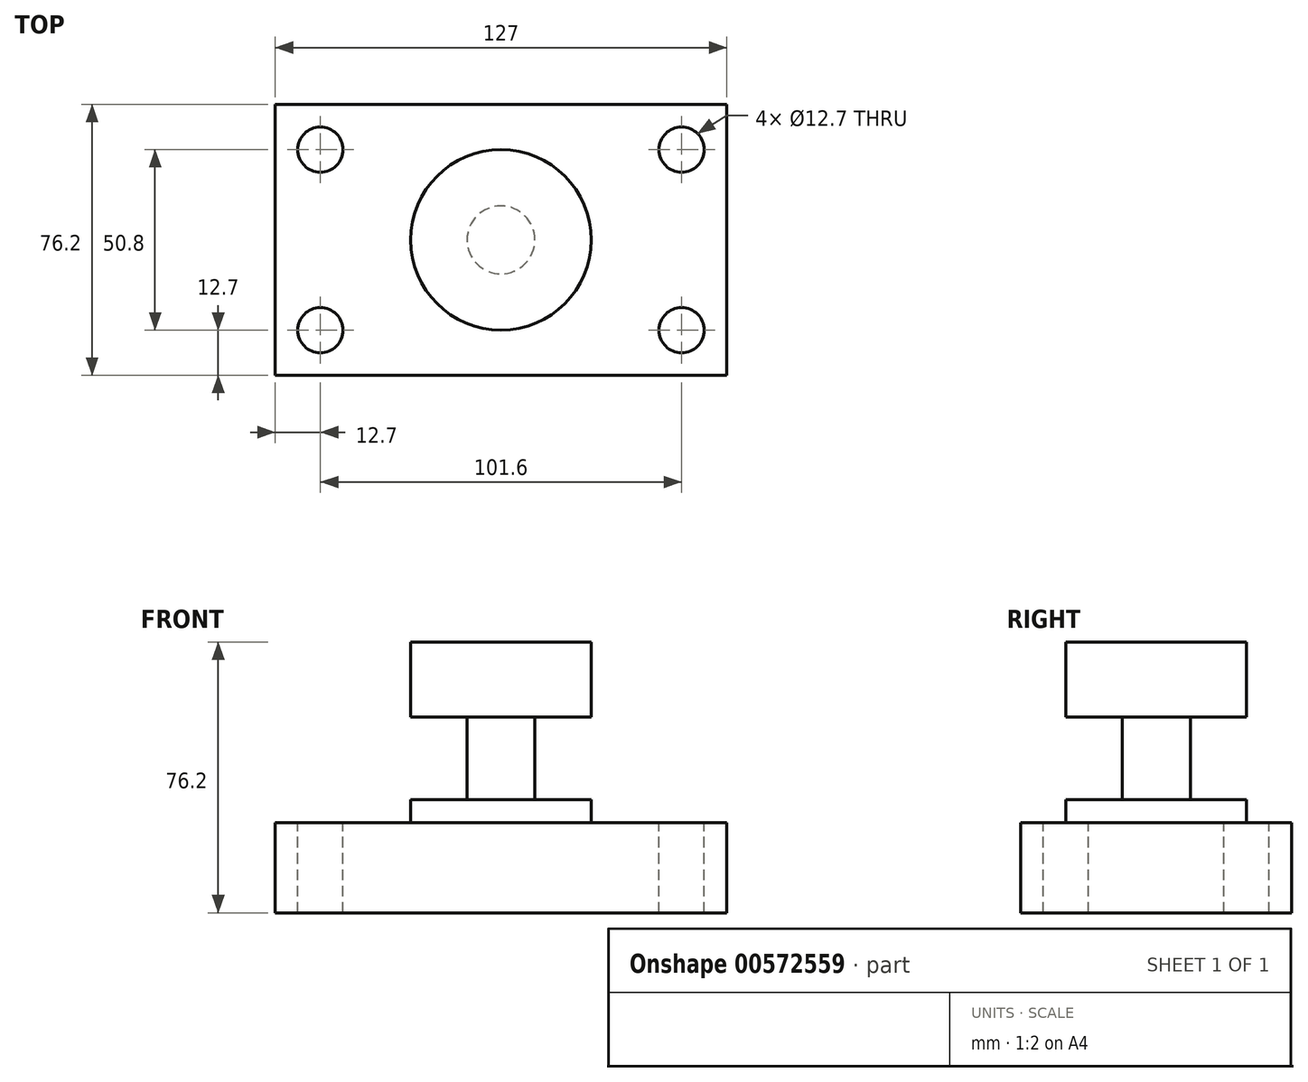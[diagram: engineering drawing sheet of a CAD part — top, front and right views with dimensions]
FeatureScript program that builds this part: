
annotation { "Feature Type Name" : "Feature", "Feature Type Description" : "" }
export const myFeature = defineFeature(function(context is Context, id is Id, definition is map)
    precondition{}
    {
        {
            var Q0;
            Q0=qCreatedBy(makeId("Top.planeOp"),FACE);
            var sketch = newSketch(context, id + "F0", { "sketchPlane" : qUnion([Q0])});
            skLineSegment(sketch, "E0.bottom", {"start": v(-63.5, 38.1) * mm, "end": v(63.5, 38.1) * mm});
            skLineSegment(sketch, "E0.top", {"start": v(-63.5, -38.1) * mm, "end": v(63.5, -38.1) * mm});
            skLineSegment(sketch, "E0.left", {"start": v(-63.5, 38.1) * mm, "end": v(-63.5, -38.1) * mm});
            skLineSegment(sketch, "E0.right", {"start": v(63.5, 38.1) * mm, "end": v(63.5, -38.1) * mm});
            skPoint(sketch, "E0.middle", {"position": v(0, 0) * mm});
            skSolve(sketch);
        }
        {
            var Q0;
            Q0 = qSketchRegion(id + "F0", true);
            extrude(context, id + "F1", {"entities" : qUnion([Q0]), "depth" : 25.4 * mm, "offsetDistance" : 25.4 * mm});
        }
        {
            var Q0;
            Q0=makeQuery(id+"F1.opExtrude","CAP_FACE",FACE,{"disambiguationData":[OSD([sQuery(id+"F0.wireOp",EDGE,"E0.bottom"),sQuery(id+"F0.wireOp",EDGE,"E0.top"),sQuery(id+"F0.wireOp",EDGE,"E0.left"),sQuery(id+"F0.wireOp",EDGE,"E0.right")])],"isStart":false});
            var sketch = newSketch(context, id + "F2", { "sketchPlane" : qUnion([Q0])});
            skCircle(sketch, "E1", {"center": v(50.8, -25.4) * mm, "radius": 6.35 * mm});
            skCircle(sketch, "E2", {"center": v(-50.8, -25.4) * mm, "radius": 6.35 * mm});
            skCircle(sketch, "E3", {"center": v(50.8, 25.4) * mm, "radius": 6.35 * mm});
            skCircle(sketch, "E4", {"center": v(-50.8, 25.4) * mm, "radius": 6.35 * mm});
            skSolve(sketch);
        }
        {
            var Q0;
            Q0 = qSketchRegion(id + "F2", true);
            extrude(context, id + "F3", {"entities" : qUnion([Q0]), "operationType" : NewBodyOperationType.REMOVE, "oppositeDirection" : true, "depth" : 25.4 * mm, "offsetDistance" : 25.4 * mm});
        }
        {
            var Q0;
            Q0=qCreatedBy(makeId("Front.planeOp"),FACE);
            var sketch = newSketch(context, id + "F4", { "sketchPlane" : qUnion([Q0])});
            skLineSegment(sketch, "E5.bottom", {"start": v(0, 25.4) * mm, "end": v(-25.4, 25.4) * mm});
            skLineSegment(sketch, "E5.top", {"start": v(0, 76.2) * mm, "end": v(-25.4, 76.2) * mm});
            skLineSegment(sketch, "E5.left", {"start": v(0, 25.4) * mm, "end": v(0, 76.2) * mm});
            skLineSegment(sketch, "E5.right", {"start": v(-25.4, 25.4) * mm, "end": v(-25.4, 76.2) * mm});
            skSolve(sketch);
        }
        {
            var Q0;
            Q0=makeQuery(id+"F4.imprint","IMPRINT",FACE,{"disambiguationData":[TD([[makeQuery(id+"F4.imprint","IMPRINT",EDGE,{"derivedFrom":sQuery(id+"F4.wireOp",EDGE,"E5.bottom")}),-1.0]])]});
            var Q1;
            Q1=sQuery(id+"F4.wireOp",EDGE,"E5.left");
            revolve(context, id + "F5", {"operationType" : NewBodyOperationType.ADD, "entities" : qUnion([Q0]), "axis" : qUnion([Q1]), "revolveType" : RevolveType.FULL});
        }
        {
            var Q0;
            Q0=qCreatedBy(makeId("Front.planeOp"),FACE);
            var sketch = newSketch(context, id + "F6", { "sketchPlane" : qUnion([Q0])});
            skLineSegment(sketch, "E6.bottom", {"start": v(9.54, 55.03) * mm, "end": v(60.18, 55.03) * mm});
            skLineSegment(sketch, "E6.top", {"start": v(9.54, 31.84) * mm, "end": v(60.18, 31.84) * mm});
            skLineSegment(sketch, "E6.left", {"start": v(9.54, 55.03) * mm, "end": v(9.54, 31.84) * mm});
            skLineSegment(sketch, "E6.right", {"start": v(60.18, 55.03) * mm, "end": v(60.18, 31.84) * mm});
            skSolve(sketch);
        }
        {
            var Q0;
            Q0 = qSketchRegion(id + "F6", true);
            var Q1;
            Q1=makeQuery(id+"F5.opRevolve","SWEPT_FACE",FACE,{"disambiguationData":[OSD([sQuery(id+"F4.wireOp",EDGE,"E5.right")])]});
            revolve(context, id + "F7", {"operationType" : NewBodyOperationType.REMOVE, "entities" : qUnion([Q0]), "axis" : qUnion([Q1]), "revolveType" : RevolveType.FULL});
        }
    });
